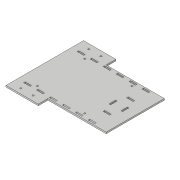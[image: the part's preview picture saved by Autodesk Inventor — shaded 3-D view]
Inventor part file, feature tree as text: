
AUTODESK INVENTOR PART (.ipt)
format: ipt  version: 2017 (Build 210142000, 142)  size: 234,496 bytes
history: native  units: in
note: dims shown in document units (in); Inventor stores cm internally (conversion verified against a paired STEP export)
features: extrude x6, sketch x6
ambient origin geometry x8: Origin, YZ Plane, XZ Plane, XY Plane, X Axis, Y Axis, Z Axis, Center Point
bodies: Solid1 (feature_tree)
feature tree (12):
  extrude  "Extrusion1"  Depth=7.0in
  extrude  "Extrusion2"  Depth=0.115in
  extrude  "Extrusion3"  Depth=1.9685in
  extrude  "Extrusion4"  Depth=0.125in
  extrude  "Extrusion5"  Depth=0.125in
  extrude  "Extrusion6"  Depth=0.115in
  sketch  "Sketch1"  dims[d0=4.5in d1=7.0in]
  sketch  "Sketch2"  dims[d6=0.115in d7=0.0in d8=3.937in]
  sketch  "Sketch4"  dims[d9=3.937in d10=1.9685in]
  sketch  "Sketch5"  dims[d11=2.375in d12=0.125in]
  sketch  "Sketch6"  dims[d13=0.125in d14=0.125in]
  sketch  "Sketch7"  dims[d15=0.125in d16=0.14in d17=0.14in d18=0.14in d19=0.14in d20=0.14in d21=0.14in d22=0.14in d23=0.14in d24=1.0in d25=0.0in d26=0.115in d27=0.115in d28=0.115in d29=0.5in d30=0.5in d31=0.5in d32=0.115in d33=0.5in d34=2.3622in d36=1.0in d37=0.3937in d39=1.0in d41=1.0in d42=0.0in d43=2.5in d44=0.75in d45=2.5in d46=0.75in d47=0.0in d48=0.115in d49=0.0in d50=0.125in d51=0.375in d52=0.375in d53=0.95in d54=0.95in d55=0.375in d56=0.375in d57=0.125in d58=0.125in d59=0.125in d61=0.775in d62=0.115in d63=0.0in d64=0.0in d65=0.775in d66=1.7in d67=0.5in d68=0.835in d69=0.115in d70=0.115in d71=2.0in d72=0.5in d73=0.25in d74=0.8in d75=0.115in d76=0.115in d77=0.15in d78=0.115in d79=0.0in]
